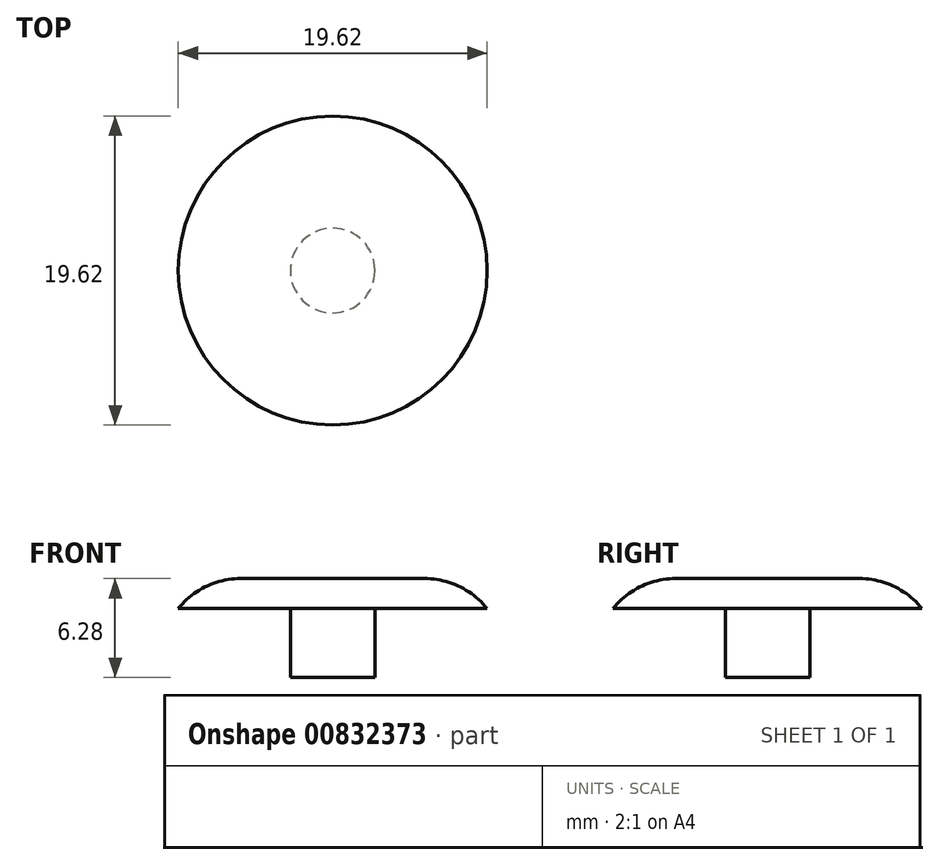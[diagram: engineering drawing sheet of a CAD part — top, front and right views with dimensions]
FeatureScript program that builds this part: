
annotation { "Feature Type Name" : "Feature", "Feature Type Description" : "" }
export const myFeature = defineFeature(function(context is Context, id is Id, definition is map)
    precondition{}
    {
        {
            var Q0;
            Q0=qCreatedBy(makeId("Top.planeOp"),FACE);
            var sketch = newSketch(context, id + "F0", { "sketchPlane" : qUnion([Q0])});
            skCircle(sketch, "E0", {"center": v(0, 0) * mm, "radius": 9.8 * mm, "construction": true});
            skCircle(sketch, "E1", {"center": v(0, 0) * mm, "radius": 2.7 * mm, "construction": true});
            skCircle(sketch, "E2", {"center": v(0, 0) * mm, "radius": 9.8 * mm});
            skCircle(sketch, "E3", {"center": v(0, 0) * mm, "radius": 2.69 * mm});
            skSolve(sketch);
        }
        {
            var Q0;
            Q0=makeQuery(id+"F0.imprint","IMPRINT",FACE,{"disambiguationData":[TD([[makeQuery(id+"F0.imprint","IMPRINT",EDGE,{"derivedFrom":sQuery(id+"F0.wireOp",EDGE,"E2")}),1.0]])]});
            var Q1;
            Q1=makeQuery(id+"F0.imprint","IMPRINT",FACE,{"disambiguationData":[TD([[makeQuery(id+"F0.imprint","IMPRINT",EDGE,{"derivedFrom":sQuery(id+"F0.wireOp",EDGE,"E3")}),1.0]])]});
            extrude(context, id + "F1", {"entities" : qUnion([Q0, Q1]), "depth" : 1.9 * mm, "offsetDistance" : 25.4 * mm});
        }
        {
            var Q0;
            Q0=makeQuery(id+"F0.imprint","IMPRINT",FACE,{"disambiguationData":[TD([[makeQuery(id+"F0.imprint","IMPRINT",EDGE,{"derivedFrom":sQuery(id+"F0.wireOp",EDGE,"E3")}),1.0]])]});
            extrude(context, id + "F2", {"entities" : qUnion([Q0]), "operationType" : NewBodyOperationType.ADD, "oppositeDirection" : true, "depth" : 4.37 * mm, "offsetDistance" : 25.4 * mm});
        }
        {
            var Q0;
            Q0=makeQuery(id+"F1.opExtrude","CAP_EDGE",EDGE,{"disambiguationData":[OSD([sQuery(id+"F0.wireOp",EDGE,"E2")])],"isStart":false});
            fillet(context, id + "F3", {"entities" : qUnion([Q0]), "radius" : 5.08 * mm, "tangentPropagation" : true, "allowEdgeOverflow" : false});
        }
    });
